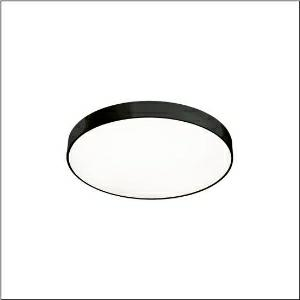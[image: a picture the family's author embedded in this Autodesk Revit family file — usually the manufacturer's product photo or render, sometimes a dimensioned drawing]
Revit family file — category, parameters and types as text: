
# Revit family: round_21_m_51mr36fm8421b
name_source: partatom
category: Lighting Fixtures
units: mm (PartAtom-declared; Revit-internal decimal feet)

## family parameters
Cut with Voids When Loaded = No
Host = Face
Light Source = No
Part Type = Normal
Room Calculation Point = No
Round Connector Dimension = Use Diameter
Shared = No

## types (1)
- --- (1 x LED, 8900 lm, 62.6 W, 4000K)
    Apparent Load = 63 VA
    CIE Flux Codes = 49 80 96 100 100
    Color Rendering = 80
    Color Temperature = 4000K
    Default Elevation = 1800 mm
    Description = Round 21 M, wall and ceiling luminaire, primary optical cover: cover, of PMMA, opal, light emission: direct distribution, primary light characteristic: symmetric, installation type: surface-mounted, suspended mounting, LED, rated luminous flux: 8.140lm, luminous efficacy: 133lm/W, light colour: 840, colour temperature: 4000K, control gear: ON/OFF Multilumen, with terminal, 3-pole, mains connection: 230V, AC, 50/60Hz, rated input power: 61W, housing, of aluminium, coated, black, diameter: 600mm, height: 62mm, protection rating (complete): IP40, insulation class (complete): insulation class I (protective earthing), certification: CE, impact resistance: IK04, permissible operating ambient temperature: -10..+35°C, packaging unit: 1 piece
    Height = 87 mm
    Lamp = 1 x LED
    Lamp Light Flux = 8900 lm
    Lamp Power = 62.6 W
    Lamp count = 1
    Length = 600 mm
    Luminous efficacy = 142 lm/W
    Manufacturer = Siteco
    ModVariant = No
    Model = 51MR36FM8421B
    Mounting Place = Ceiling
    Mounting Type = Surface mounted
    Number of Poles = 1
    OnlyDefault = Yes
    Power Factor = 1
    Product Name = Round 21 M
    Product group = wall and ceiling luminaire
    ProductGroupID = 304
    Protection Class = Protection class I
    Protection Degree = IP 40
    RLX_Detail_Level = 1
    RLX_Emergency_Light_Flux = 0 lm
    RLX_Emergency_Type = 0
    RLX_Emergency_Type_DB = No
    RlxData = <blob elided: 20413 chars, md5=7713db31>
    Socket = socket
    Standby Power = 0 W
    System Light Flux = 8900 lm
    System Power = 63 W
    Type Comments = factory setting: luminous flux: 100 % | (ON | ON | ON | ON) | 700 mA
    Type Image = l_1258332.jpg
    URL = http://relux.com
    VarID = @adj_032878
    Voltage = 0 V
    Weight = 0.00 kg
    Width = 0 mm  [stored 0 ft]

note: [stored X ft] marks values corroborated as IEEE doubles in the binary element streams (Revit-internal decimal feet)

## geometry (parser evidence)
native form markers: Blend x4, Sweep x12
no freeform markers — native parametric forms only
